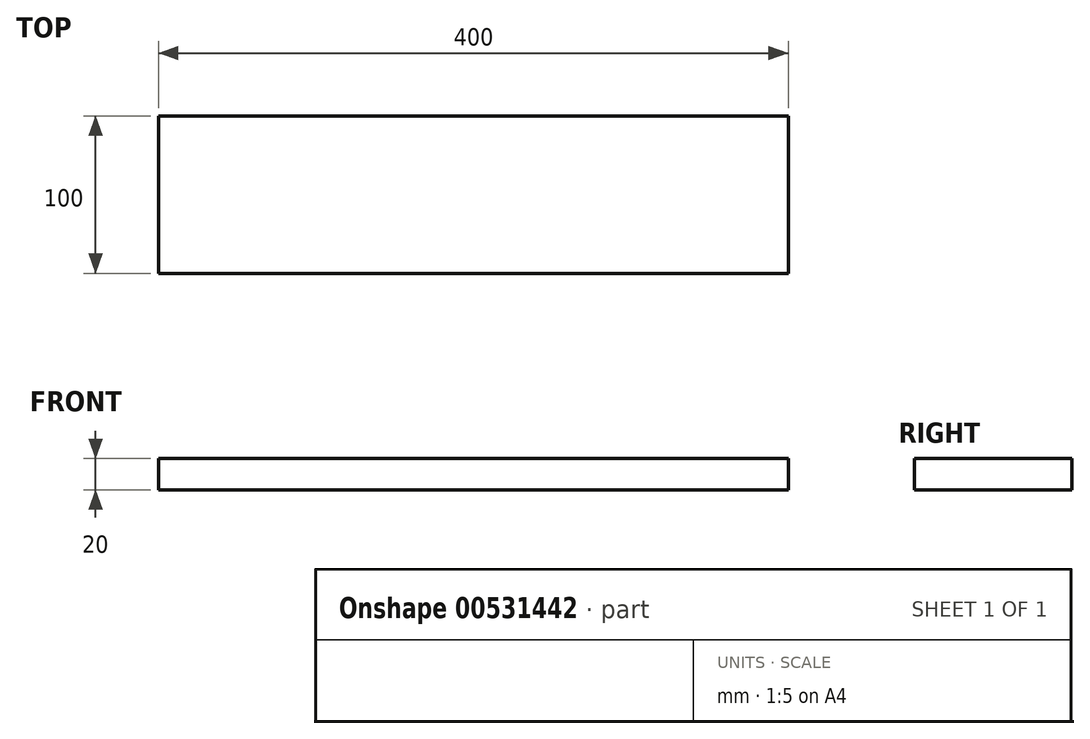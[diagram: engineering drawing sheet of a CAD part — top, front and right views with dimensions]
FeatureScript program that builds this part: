
annotation { "Feature Type Name" : "Feature", "Feature Type Description" : "" }
export const myFeature = defineFeature(function(context is Context, id is Id, definition is map)
    precondition{}
    {
        {
            var Q0;
            Q0=qCreatedBy(makeId("Right.planeOp"),FACE);
            var sketch = newSketch(context, id + "F0", { "sketchPlane" : qUnion([Q0])});
            skLineSegment(sketch, "E0.bottom", {"start": v(50, 10) * mm, "end": v(-50, 10) * mm});
            skLineSegment(sketch, "E0.top", {"start": v(50, -10) * mm, "end": v(-50, -10) * mm});
            skLineSegment(sketch, "E0.left", {"start": v(50, 10) * mm, "end": v(50, -10) * mm});
            skLineSegment(sketch, "E0.right", {"start": v(-50, 10) * mm, "end": v(-50, -10) * mm});
            skPoint(sketch, "E0.middle", {"position": v(0, 0) * mm});
            skSolve(sketch);
        }
        {
            var Q0;
            Q0=makeQuery(id+"F0.imprint","IMPRINT",FACE,{"disambiguationData":[TD([[makeQuery(id+"F0.imprint","IMPRINT",EDGE,{"derivedFrom":sQuery(id+"F0.wireOp",EDGE,"E0.bottom")}),1.0]])]});
            extrude(context, id + "F1", {"entities" : qUnion([Q0]), "endBound" : BoundingType.SYMMETRIC, "depth" : 400 * mm, "offsetDistance" : 25 * mm});
        }
    });
